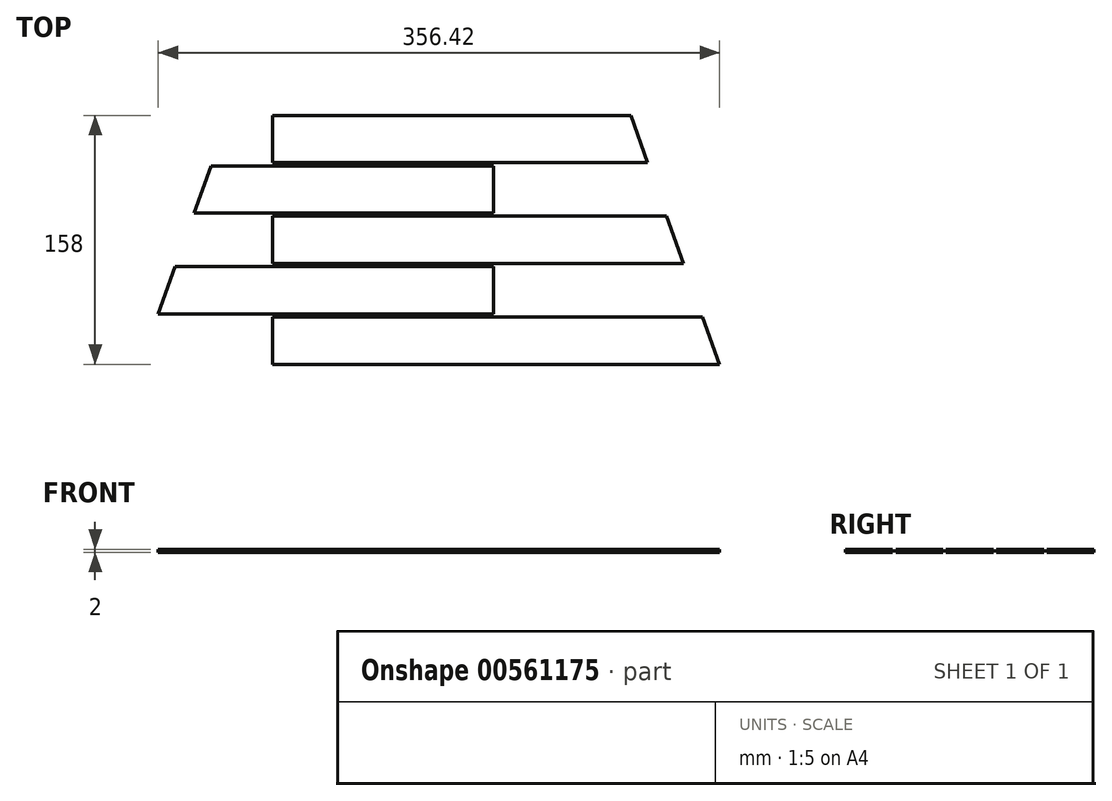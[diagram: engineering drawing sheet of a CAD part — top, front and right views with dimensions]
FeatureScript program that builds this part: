
annotation { "Feature Type Name" : "Feature", "Feature Type Description" : "" }
export const myFeature = defineFeature(function(context is Context, id is Id, definition is map)
    precondition{}
    {
        {
            var Q0;
            Q0=qCreatedBy(makeId("Top.planeOp"),FACE);
            var sketch = newSketch(context, id + "F0", { "sketchPlane" : qUnion([Q0])});
            skLineSegment(sketch, "E0", {"start": v(-183.9, -235.5) * mm, "end": v(-100, 0) * mm});
            skLineSegment(sketch, "E1", {"start": v(-100, 0) * mm, "end": v(100, 0) * mm});
            skLineSegment(sketch, "E2", {"start": v(100, 0) * mm, "end": v(183.9, -235.5) * mm});
            skLineSegment(sketch, "E3", {"start": v(-105, 30) * mm, "end": v(-105, 280) * mm});
            skLineSegment(sketch, "E4", {"start": v(-105, 280) * mm, "end": v(105, 280) * mm});
            skLineSegment(sketch, "E5", {"start": v(105, 280) * mm, "end": v(105, 30) * mm});
            skSolve(sketch);
        }
        {
            var Q0;
            Q0 = qSketchRegion(id + "F0", true);
            var Q1;
            Q1 = qSketchRegion(id + "F0", true);
            var Q2;
            Q2=sQuery(id+"F0.wireOp",EDGE,"E3");
            var Q3;
            Q3=sQuery(id+"F0.wireOp",EDGE,"E4");
            var Q4;
            Q4=sQuery(id+"F0.wireOp",EDGE,"E5");
            var Q5;
            Q5=sQuery(id+"F0.wireOp",EDGE,"E2");
            var Q6;
            Q6=sQuery(id+"F0.wireOp",EDGE,"E1");
            var Q7;
            Q7=sQuery(id+"F0.wireOp",EDGE,"E0");
            extrude(context, id + "F1", {"entities" : qUnion([Q0]), "bodyType" : ToolBodyType.SURFACE, "surfaceEntities" : qUnion([Q1, Q2, Q3, Q4, Q5, Q6, Q7]), "depth" : 250 * mm, "offsetDistance" : 25 * mm});
        }
        {
            var Q0;
            Q0=qCreatedBy(makeId("Top.planeOp"),FACE);
            var sketch = newSketch(context, id + "F2", { "sketchPlane" : qUnion([Q0])});
            skLineSegment(sketch, "E6", {"start": v(183.9, -235.5) * mm, "end": v(-99.78, -235.5) * mm});
            skLineSegment(sketch, "E7", {"start": v(-99.78, -235.5) * mm, "end": v(-99.78, -205.5) * mm});
            skLineSegment(sketch, "E8", {"start": v(-99.78, -205.5) * mm, "end": v(173.22, -205.5) * mm});
            skLineSegment(sketch, "E9", {"start": v(173.22, -205.5) * mm, "end": v(183.9, -235.5) * mm});
            skLineSegment(sketch, "E10", {"start": v(-172.5, -203.5) * mm, "end": v(40.53, -203.5) * mm});
            skLineSegment(sketch, "E11", {"start": v(40.53, -203.5) * mm, "end": v(40.53, -173.5) * mm});
            skLineSegment(sketch, "E12", {"start": v(40.53, -173.5) * mm, "end": v(-161.82, -173.5) * mm});
            skLineSegment(sketch, "E13", {"start": v(-161.82, -173.5) * mm, "end": v(-172.5, -203.5) * mm});
            skLineSegment(sketch, "E14", {"start": v(-99.78, -171.5) * mm, "end": v(-99.78, -141.5) * mm});
            skLineSegment(sketch, "E15", {"start": v(-99.78, -141.5) * mm, "end": v(150.42, -141.5) * mm});
            skLineSegment(sketch, "E16", {"start": v(150.42, -141.5) * mm, "end": v(161.1, -171.5) * mm});
            skLineSegment(sketch, "E17", {"start": v(161.1, -171.5) * mm, "end": v(-99.78, -171.5) * mm});
            skLineSegment(sketch, "E18", {"start": v(-149.7, -139.5) * mm, "end": v(40.53, -139.5) * mm});
            skLineSegment(sketch, "E19", {"start": v(40.53, -139.5) * mm, "end": v(40.53, -109.5) * mm});
            skLineSegment(sketch, "E20", {"start": v(40.53, -109.5) * mm, "end": v(-139.01, -109.5) * mm});
            skLineSegment(sketch, "E21", {"start": v(-139.01, -109.5) * mm, "end": v(-149.7, -139.5) * mm});
            skLineSegment(sketch, "E22", {"start": v(138.3, -107.5) * mm, "end": v(-99.78, -107.5) * mm});
            skLineSegment(sketch, "E23", {"start": v(-99.78, -107.5) * mm, "end": v(-99.78, -77.5) * mm});
            skLineSegment(sketch, "E24", {"start": v(-99.78, -77.5) * mm, "end": v(127.61, -77.5) * mm});
            skLineSegment(sketch, "E25", {"start": v(127.61, -77.5) * mm, "end": v(138.3, -107.5) * mm});
            skSolve(sketch);
        }
        {
            var Q0;
            Q0 = qSketchRegion(id + "F2", true);
            extrude(context, id + "F3", {"entities" : qUnion([Q0]), "depth" : 2 * mm, "offsetDistance" : 25 * mm});
        }
    });
